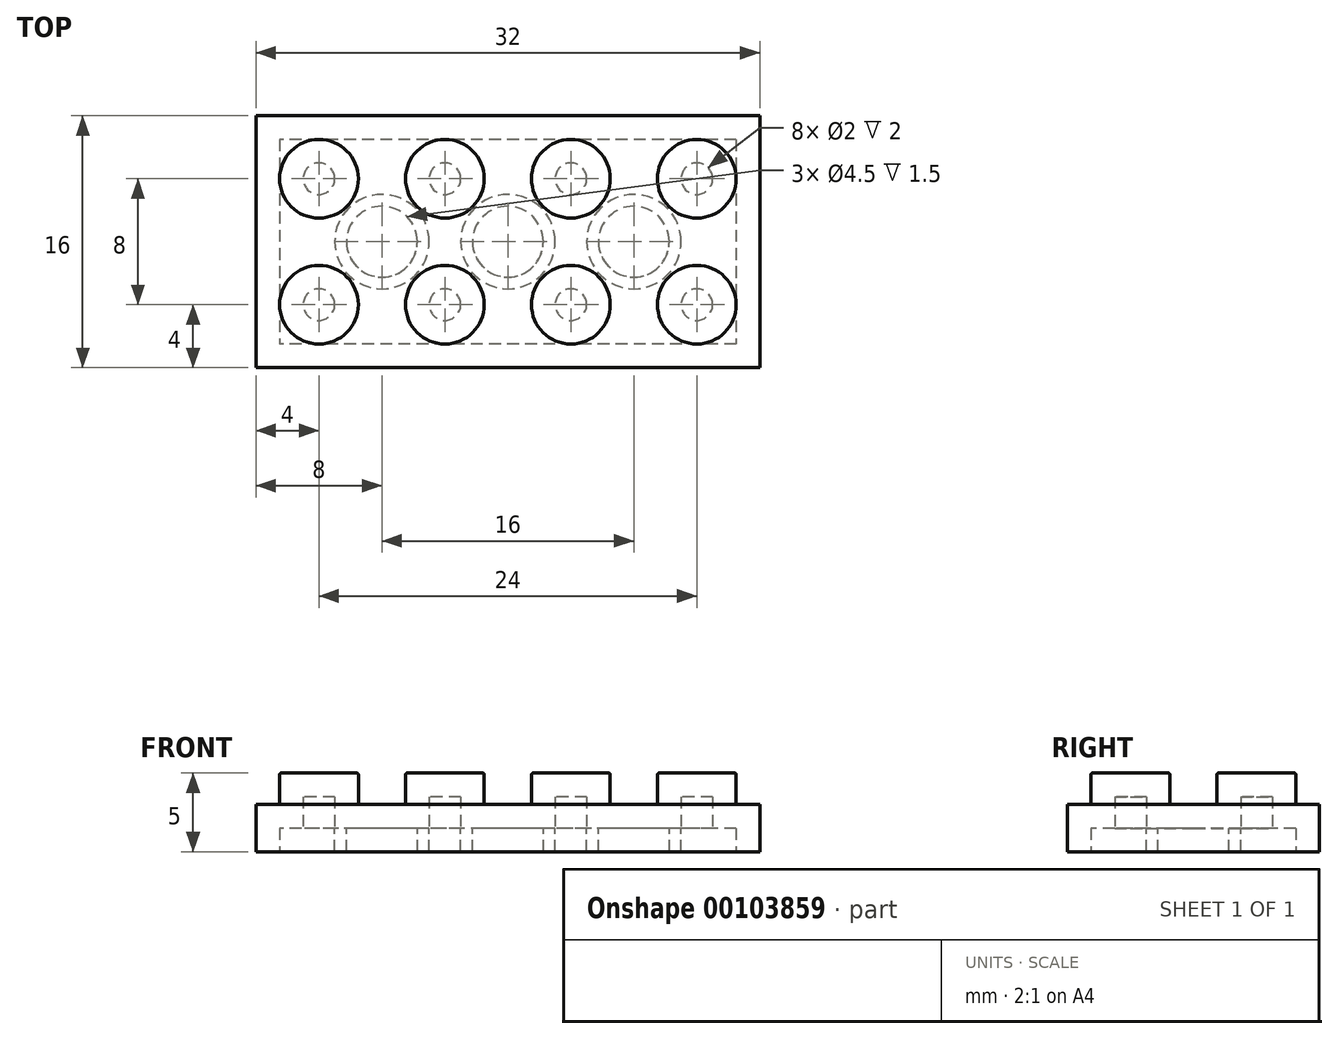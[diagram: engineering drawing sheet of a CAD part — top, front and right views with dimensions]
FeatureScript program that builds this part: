
annotation { "Feature Type Name" : "Feature", "Feature Type Description" : "" }
export const myFeature = defineFeature(function(context is Context, id is Id, definition is map)
    precondition{}
    {
        {
            var Q0;
            Q0=qCreatedBy(makeId("Top.planeOp"),FACE);
            var sketch = newSketch(context, id + "F0", { "sketchPlane" : qUnion([Q0])});
            skLineSegment(sketch, "E0.bottom", {"start": v(16, 8) * mm, "end": v(-16, 8) * mm});
            skLineSegment(sketch, "E0.top", {"start": v(16, -8) * mm, "end": v(-16, -8) * mm});
            skLineSegment(sketch, "E0.left", {"start": v(16, 8) * mm, "end": v(16, -8) * mm});
            skLineSegment(sketch, "E0.right", {"start": v(-16, 8) * mm, "end": v(-16, -8) * mm});
            skPoint(sketch, "E0.middle", {"position": v(0, 0) * mm});
            skSolve(sketch);
        }
        {
            var Q0;
            Q0=makeQuery(id+"F0.imprint","IMPRINT",FACE,{"disambiguationData":[TD([[makeQuery(id+"F0.imprint","IMPRINT",EDGE,{"derivedFrom":sQuery(id+"F0.wireOp",EDGE,"E0.bottom")}),1.0]])]});
            extrude(context, id + "F1", {"entities" : qUnion([Q0]), "depth" : 3 * mm});
        }
        {
            var Q0;
            Q0=makeQuery(id+"F1.opExtrude","CAP_FACE",FACE,{"disambiguationData":[OSD([sQuery(id+"F0.wireOp",EDGE,"E0.bottom"),sQuery(id+"F0.wireOp",EDGE,"E0.top"),sQuery(id+"F0.wireOp",EDGE,"E0.left"),sQuery(id+"F0.wireOp",EDGE,"E0.right")])],"isStart":false});
            var sketch = newSketch(context, id + "F2", { "sketchPlane" : qUnion([Q0])});
            skCircle(sketch, "E1", {"center": v(-12, 4) * mm, "radius": 2.5 * mm});
            skCircle(sketch, "E2.0.1.0", {"center": v(-12, -4) * mm, "radius": 2.5 * mm});
            skCircle(sketch, "E2.1.0.0", {"center": v(-4, 4) * mm, "radius": 2.5 * mm});
            skCircle(sketch, "E2.1.1.0", {"center": v(-4, -4) * mm, "radius": 2.5 * mm});
            skCircle(sketch, "E2.2.0.0", {"center": v(4, 4) * mm, "radius": 2.5 * mm});
            skCircle(sketch, "E2.2.1.0", {"center": v(4, -4) * mm, "radius": 2.5 * mm});
            skCircle(sketch, "E2.3.0.0", {"center": v(12, 4) * mm, "radius": 2.5 * mm});
            skCircle(sketch, "E2.3.1.0", {"center": v(12, -4) * mm, "radius": 2.5 * mm});
            skLineSegment(sketch, "E2.direction1", {"start": v(-12, 4) * mm, "end": v(-4, 4) * mm, "construction": true});
            skLineSegment(sketch, "E2.direction2", {"start": v(-12, 4) * mm, "end": v(-12, -4) * mm, "construction": true});
            skLineSegment(sketch, "E3", {"start": v(4, 4) * mm, "end": v(-4, -4) * mm, "construction": true});
            skSolve(sketch);
        }
        {
            var Q0;
            Q0 = qSketchRegion(id + "F2", true);
            extrude(context, id + "F3", {"entities" : qUnion([Q0]), "operationType" : NewBodyOperationType.ADD, "depth" : 2 * mm});
        }
        {
            var Q0;
            Q0=makeQuery(id+"F3.opExtrude","CAP_EDGE",EDGE,{"disambiguationData":[OSD([sQuery(id+"F2.wireOp",EDGE,"E1")])],"isStart":false});
            var Q1;
            Q1=makeQuery(id+"F3.opExtrude","CAP_EDGE",EDGE,{"disambiguationData":[OSD([sQuery(id+"F2.wireOp",EDGE,"E2.1.0.0")])],"isStart":false});
            var Q2;
            Q2=makeQuery(id+"F3.opExtrude","CAP_EDGE",EDGE,{"disambiguationData":[OSD([sQuery(id+"F2.wireOp",EDGE,"E2.2.0.0")])],"isStart":false});
            var Q3;
            Q3=makeQuery(id+"F3.opExtrude","CAP_EDGE",EDGE,{"disambiguationData":[OSD([sQuery(id+"F2.wireOp",EDGE,"E2.3.0.0")])],"isStart":false});
            var Q4;
            Q4=makeQuery(id+"F3.opExtrude","CAP_EDGE",EDGE,{"disambiguationData":[OSD([sQuery(id+"F2.wireOp",EDGE,"E2.3.1.0")])],"isStart":false});
            var Q5;
            Q5=makeQuery(id+"F3.opExtrude","CAP_EDGE",EDGE,{"disambiguationData":[OSD([sQuery(id+"F2.wireOp",EDGE,"E2.2.1.0")])],"isStart":false});
            var Q6;
            Q6=makeQuery(id+"F3.opExtrude","CAP_EDGE",EDGE,{"disambiguationData":[OSD([sQuery(id+"F2.wireOp",EDGE,"E2.1.1.0")])],"isStart":false});
            var Q7;
            Q7=makeQuery(id+"F3.opExtrude","CAP_EDGE",EDGE,{"disambiguationData":[OSD([sQuery(id+"F2.wireOp",EDGE,"E2.0.1.0")])],"isStart":false});
            fillet(context, id + "F4", {"entities" : qUnion([Q0, Q1, Q2, Q3, Q4, Q5, Q6, Q7]), "radius" : .1 * mm, "tangentPropagation" : true, "allowEdgeOverflow" : false});
        }
        {
            var Q0;
            Q0=makeQuery(id+"F1.opExtrude","CAP_FACE",FACE,{"disambiguationData":[OSD([sQuery(id+"F0.wireOp",EDGE,"E0.bottom"),sQuery(id+"F0.wireOp",EDGE,"E0.top"),sQuery(id+"F0.wireOp",EDGE,"E0.left"),sQuery(id+"F0.wireOp",EDGE,"E0.right")])],"isStart":true});
            shell(context, id + "F5", {"entities" : qUnion([Q0]), "thickness" : 1.5 * mm});
        }
        {
            var Q0;
            Q0=makeQuery(id+"F5.opShell","OFFSET_FACE",FACE,{"disambiguationData":[OSD([sQuery(id+"F0.wireOp",EDGE,"E0.bottom"),sQuery(id+"F0.wireOp",EDGE,"E0.top"),sQuery(id+"F0.wireOp",EDGE,"E0.left"),sQuery(id+"F0.wireOp",EDGE,"E0.right")])]});
            var sketch = newSketch(context, id + "F6", { "sketchPlane" : qUnion([Q0])});
            skCircle(sketch, "E4", {"center": v(-8, 0) * mm, "radius": 3 * mm});
            skCircle(sketch, "E5.0", {"center": v(-8, 0) * mm, "radius": 2.25 * mm});
            skCircle(sketch, "E6.1.0.0", {"center": v(0, 0) * mm, "radius": 2.25 * mm});
            skCircle(sketch, "E6.1.0.1", {"center": v(0, 0) * mm, "radius": 3 * mm});
            skCircle(sketch, "E6.2.0.0", {"center": v(8, 0) * mm, "radius": 2.25 * mm});
            skCircle(sketch, "E6.2.0.1", {"center": v(8, 0) * mm, "radius": 3 * mm});
            skLineSegment(sketch, "E6.direction1", {"start": v(-8, 0) * mm, "end": v(0, 0) * mm, "construction": true});
            skSolve(sketch);
        }
        {
            var Q0;
            Q0 = qSketchRegion(id + "F6", true);
            var Q1;
            Q1=makeQuery(id+"F1.opExtrude","CAP_FACE",FACE,{"disambiguationData":[OSD([sQuery(id+"F0.wireOp",EDGE,"E0.bottom"),sQuery(id+"F0.wireOp",EDGE,"E0.top"),sQuery(id+"F0.wireOp",EDGE,"E0.left"),sQuery(id+"F0.wireOp",EDGE,"E0.right")])],"isStart":true});
            extrude(context, id + "F7", {"entities" : qUnion([Q0]), "operationType" : NewBodyOperationType.ADD, "endBound" : BoundingType.UP_TO_SURFACE, "endBoundEntityFace" : qUnion([Q1]), "depth" : 25 * mm});
        }
    });
